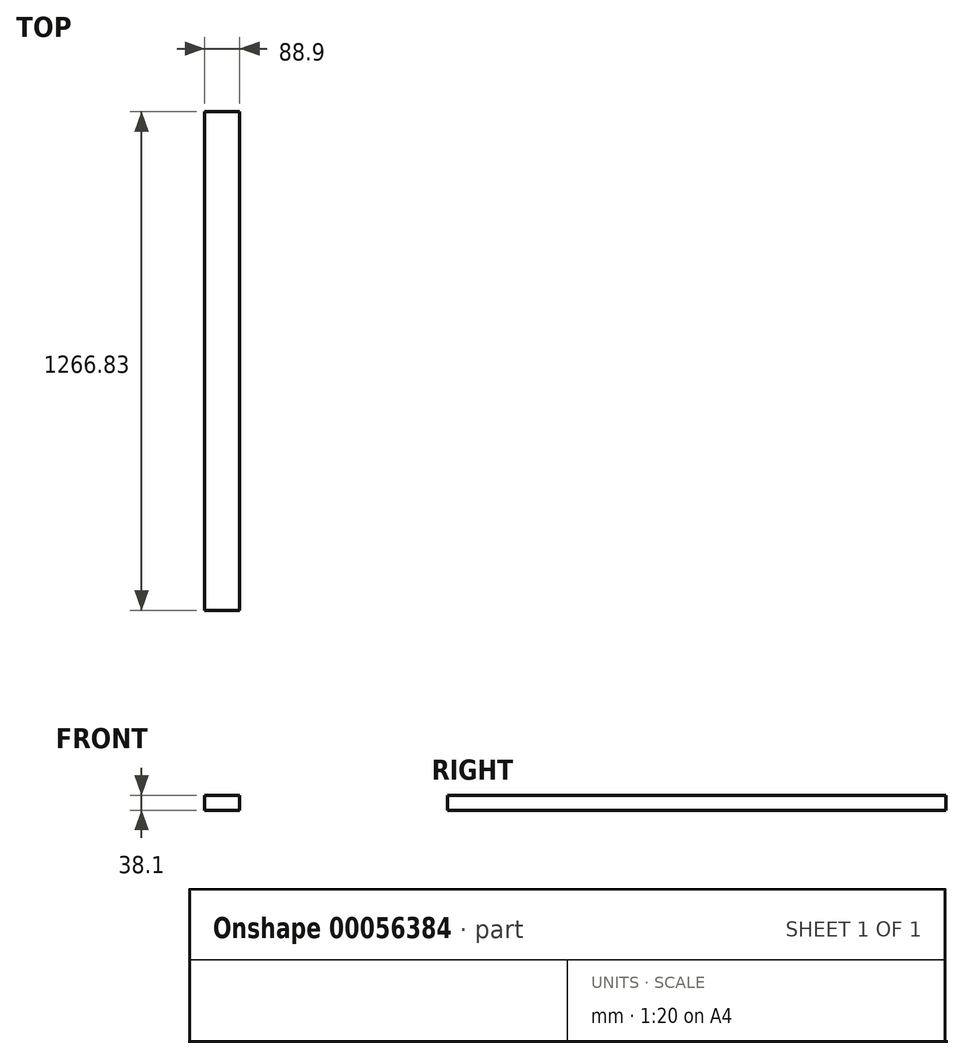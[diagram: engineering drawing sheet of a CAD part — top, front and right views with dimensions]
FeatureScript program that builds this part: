
annotation { "Feature Type Name" : "Feature", "Feature Type Description" : "" }
export const myFeature = defineFeature(function(context is Context, id is Id, definition is map)
    precondition{}
    {
        {
            var Q0;
            Q0=qCreatedBy(makeId("Front.planeOp"),FACE);
            var sketch = newSketch(context, id + "F0", { "sketchPlane" : qUnion([Q0])});
            skLineSegment(sketch, "E0.bottom", {"start": v(0, 0) * mm, "end": v(88.9, 0) * mm});
            skLineSegment(sketch, "E0.top", {"start": v(0, 38.1) * mm, "end": v(88.9, 38.1) * mm});
            skLineSegment(sketch, "E0.left", {"start": v(0, 0) * mm, "end": v(0, 38.1) * mm});
            skLineSegment(sketch, "E0.right", {"start": v(88.9, 0) * mm, "end": v(88.9, 38.1) * mm});
            skSolve(sketch);
        }
        {
            var Q0;
            Q0=makeQuery(id+"F0.imprint","IMPRINT",FACE,{"disambiguationData":[TD([[makeQuery(id+"F0.imprint","IMPRINT",EDGE,{"derivedFrom":sQuery(id+"F0.wireOp",EDGE,"E0.bottom")}),1.0]])]});
            extrude(context, id + "F1", {"entities" : qUnion([Q0]), "depth" : 1266.82 * mm});
        }
    });
